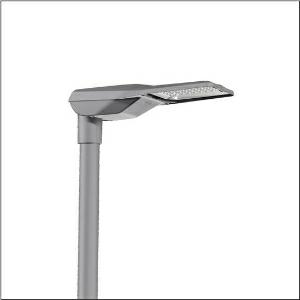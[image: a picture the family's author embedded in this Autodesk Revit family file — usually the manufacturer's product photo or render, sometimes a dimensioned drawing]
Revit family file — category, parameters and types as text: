
# Revit family: streetlight_sl_21_iq_mini___st0_8a_5xe2c61g08hb_b958
name_source: partatom
category: Lighting Fixtures
units: mm (PartAtom-declared; Revit-internal decimal feet)

## family parameters
Cut with Voids When Loaded = No
Host = Face
Light Source = No
Part Type = Normal
Room Calculation Point = No
Round Connector Dimension = Use Diameter
Shared = No

## types (1)
- --- (1 x LED, 8480 lm, 70.9 W, 2700K)
    Apparent Load = 71 VA
    CIE Flux Codes = 38 75 97 100 100
    Color Rendering = 70
    Color Temperature = 2700K
    Default Elevation = 1800 mm
    Description = Streetlight SL 21 mini, mast luminaire, primary light control with lens, of PMMA, primary optical cover: cover, of toughened safety glass, transparent, light distribution: ST0.8a, light emission: direct distribution, primary light characteristic: asymmetric, installation type: post-top, side-entry, LED, High Power LED, rated luminous flux: 8.480lm, luminous efficacy: 120lm/W, light colour: 727, colour temperature: 2700K, control gear: ECG iQ, control: Street-Remote, Auto-Match, Temp-Guard, Lumen-Switch, Night-Set, Smart-Wire, Light-Fading, Desk-Remote (wireless, voltage-free reading and setting of iQ features in the workshop via application-optimized NFC function/RFID function), optimised constant luminous flux control (CLO 2.0), mains connection: 220..240V, AC, 50/60Hz, start of lifetime: 71W, end of lifetime: 75W, reduction: 31W, luminaire housing, of diecast aluminium, powder-coated, Siteco® metallic grey (DB 702S), corrosivity category C5 according to DIN EN ISO 12944, length: 628mm, width: 235mm, height: 110mm, spigot size: 60/76mm (post-top) and 42/60/76mm (side-entry), mast flange for spigot size: 42mm: 5XC10008XM4, 60mm: 5XC10008XM2, 76/60mm: 5XC10108XM1, protection rating (complete): IP66, insulation class (complete): insulation class II (safety insulation), certification: CE, ENEC, VDE, impact resistance: IK09, permissible operating ambient temperature for outdoor applications: -40..+50°C, standard-compliant lighting for roads and squares, packaging unit: 1 piece

Light Distribution: ST0.8a
    Height = 110 mm
    Lamp = 1 x LED
    Lamp Light Flux = 8480 lm
    Lamp Power = 70.9 W
    Lamp count = 1
    Length = 625 mm
    Luminous efficacy = 120 lm/W
    Manufacturer = Siteco
    ModVariant = No
    Model = 5XE2C61G08HB
    Number of Poles = 1
    OnlyDefault = Yes
    Power Factor = 1
    Product Name = Streetlight SL 21 iQ mini | ST0.8a
    Product group = mast luminaire | pylon top
    ProductGroupID = 6100
    Protection Class = Protection class II
    Protection Degree = IP 66
    RLX_Detail_Level = 1
    RlxData = <blob elided: 91885 chars, md5=f1c289e7>
    Socket = socket
    Standby Power = 0 W
    System Light Flux = 8480 lm
    System Power = 71 W
    Type Comments = factory setting: luminous flux: 100 % | dim-lin: 254 | 711 mA
    Type Image = l_1003519.jpg
    URL = http://relux.com
    VarID = @adj_068733
    Voltage = 0 V
    Weight = 0.00 kg
    Width = 234 mm

## geometry (parser evidence)
native form markers: Blend x4, Sweep x12
no freeform markers — native parametric forms only
